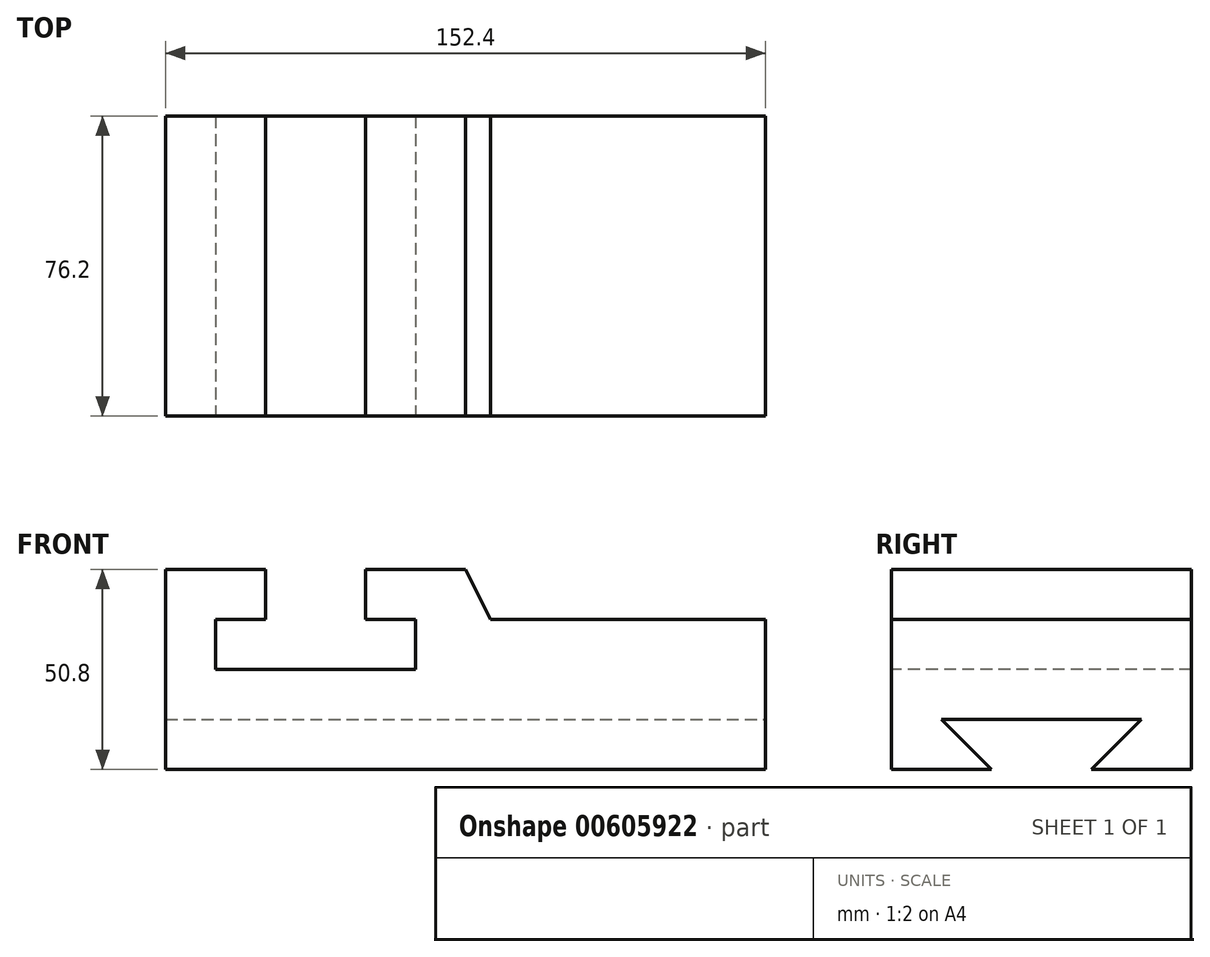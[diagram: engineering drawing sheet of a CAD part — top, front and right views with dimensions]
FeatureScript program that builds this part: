
annotation { "Feature Type Name" : "Feature", "Feature Type Description" : "" }
export const myFeature = defineFeature(function(context is Context, id is Id, definition is map)
    precondition{}
    {
        {
            var Q0;
            Q0=qCreatedBy(makeId("Front.planeOp"),FACE);
            var sketch = newSketch(context, id + "F0", { "sketchPlane" : qUnion([Q0])});
            skLineSegment(sketch, "E0", {"start": v(0, 0) * mm, "end": v(152.4, 0) * mm});
            skLineSegment(sketch, "E1", {"start": v(152.4, 0) * mm, "end": v(152.4, 50.8) * mm});
            skLineSegment(sketch, "E2", {"start": v(152.4, 50.8) * mm, "end": v(0, 50.8) * mm});
            skLineSegment(sketch, "E3", {"start": v(0, 50.8) * mm, "end": v(0, 0) * mm});
            skSolve(sketch);
        }
        {
            var Q0;
            Q0 = qSketchRegion(id + "F0", true);
            extrude(context, id + "F1", {"entities" : qUnion([Q0]), "depth" : 76.2 * mm, "offsetDistance" : 25.4 * mm});
        }
        {
            var Q0;
            Q0=makeQuery(id+"F1.opExtrude","SWEPT_FACE",FACE,{"disambiguationData":[OSD([sQuery(id+"F0.wireOp",EDGE,"E1")])]});
            var sketch = newSketch(context, id + "F2", { "sketchPlane" : qUnion([Q0])});
            skLineSegment(sketch, "E4", {"start": v(-38.1, 0) * mm, "end": v(-50.8, 0) * mm});
            skLineSegment(sketch, "E5", {"start": v(-50.8, 0) * mm, "end": v(-25.4, 0) * mm});
            skLineSegment(sketch, "E6", {"start": v(-38.1, 12.7) * mm, "end": v(-63.5, 12.7) * mm});
            skLineSegment(sketch, "E7", {"start": v(-38.1, 12.7) * mm, "end": v(-12.7, 12.7) * mm});
            skLineSegment(sketch, "E8", {"start": v(-12.7, 12.7) * mm, "end": v(-25.4, 0) * mm});
            skLineSegment(sketch, "E9", {"start": v(-63.5, 12.7) * mm, "end": v(-50.8, 0) * mm});
            skSolve(sketch);
        }
        {
            var Q0;
            Q0=makeQuery(id+"F2.imprint","IMPRINT",FACE,{"disambiguationData":[TD([[makeQuery(id+"F2.imprint","IMPRINT",EDGE,{"derivedFrom":sQuery(id+"F2.wireOp",EDGE,"E6")}),1.0]])]});
            extrude(context, id + "F3", {"entities" : qUnion([Q0]), "operationType" : NewBodyOperationType.REMOVE, "oppositeDirection" : true, "depth" : 152.4 * mm, "offsetDistance" : 25.4 * mm});
        }
        {
            var Q0;
            Q0=makeQuery(id+"F1.opExtrude","CAP_FACE",FACE,{"disambiguationData":[OSD([sQuery(id+"F0.wireOp",EDGE,"E0"),sQuery(id+"F0.wireOp",EDGE,"E1"),sQuery(id+"F0.wireOp",EDGE,"E2"),sQuery(id+"F0.wireOp",EDGE,"E3")])],"isStart":false});
            var sketch = newSketch(context, id + "F4", { "sketchPlane" : qUnion([Q0])});
            skLineSegment(sketch, "E10", {"start": v(25.4, 50.8) * mm, "end": v(25.4, 38.1) * mm});
            skLineSegment(sketch, "E11", {"start": v(25.4, 38.1) * mm, "end": v(12.7, 38.1) * mm});
            skLineSegment(sketch, "E12", {"start": v(12.7, 38.1) * mm, "end": v(12.7, 25.4) * mm});
            skLineSegment(sketch, "E13", {"start": v(12.7, 25.4) * mm, "end": v(63.5, 25.4) * mm});
            skLineSegment(sketch, "E14", {"start": v(63.5, 25.4) * mm, "end": v(63.5, 38.1) * mm});
            skLineSegment(sketch, "E15", {"start": v(63.5, 38.1) * mm, "end": v(50.8, 38.1) * mm});
            skLineSegment(sketch, "E16", {"start": v(50.8, 38.1) * mm, "end": v(50.8, 50.8) * mm});
            skLineSegment(sketch, "E17", {"start": v(25.4, 50.8) * mm, "end": v(50.8, 50.8) * mm});
            skSolve(sketch);
        }
        {
            var Q0;
            Q0=makeQuery(id+"F4.imprint","IMPRINT",FACE,{"disambiguationData":[TD([[makeQuery(id+"F4.imprint","IMPRINT",EDGE,{"derivedFrom":sQuery(id+"F4.wireOp",EDGE,"E10")}),1.0]])]});
            extrude(context, id + "F5", {"entities" : qUnion([Q0]), "operationType" : NewBodyOperationType.REMOVE, "oppositeDirection" : true, "depth" : 76.2 * mm, "offsetDistance" : 25.4 * mm});
        }
        {
            var Q0;
            Q0=makeQuery(id+"F1.opExtrude","CAP_FACE",FACE,{"disambiguationData":[OSD([sQuery(id+"F0.wireOp",EDGE,"E0"),sQuery(id+"F0.wireOp",EDGE,"E1"),sQuery(id+"F0.wireOp",EDGE,"E2"),sQuery(id+"F0.wireOp",EDGE,"E3")])],"isStart":false});
            var sketch = newSketch(context, id + "F6", { "sketchPlane" : qUnion([Q0])});
            skLineSegment(sketch, "E18", {"start": v(50.8, 50.8) * mm, "end": v(76.2, 50.8) * mm});
            skLineSegment(sketch, "E19", {"start": v(76.2, 50.8) * mm, "end": v(82.55, 38.1) * mm});
            skLineSegment(sketch, "E20", {"start": v(82.55, 38.1) * mm, "end": v(152.4, 38.1) * mm});
            skLineSegment(sketch, "E21", {"start": v(76.2, 50.8) * mm, "end": v(152.4, 50.8) * mm});
            skSolve(sketch);
        }
        {
            var Q0;
            Q0=makeQuery(id+"F6.imprint","IMPRINT",FACE,{"disambiguationData":[TD([[makeQuery(id+"F6.imprint","IMPRINT",EDGE,{"derivedFrom":sQuery(id+"F6.wireOp",EDGE,"E19")}),1.0]])]});
            extrude(context, id + "F7", {"entities" : qUnion([Q0]), "operationType" : NewBodyOperationType.REMOVE, "oppositeDirection" : true, "depth" : 76.2 * mm, "offsetDistance" : 25.4 * mm});
        }
    });
